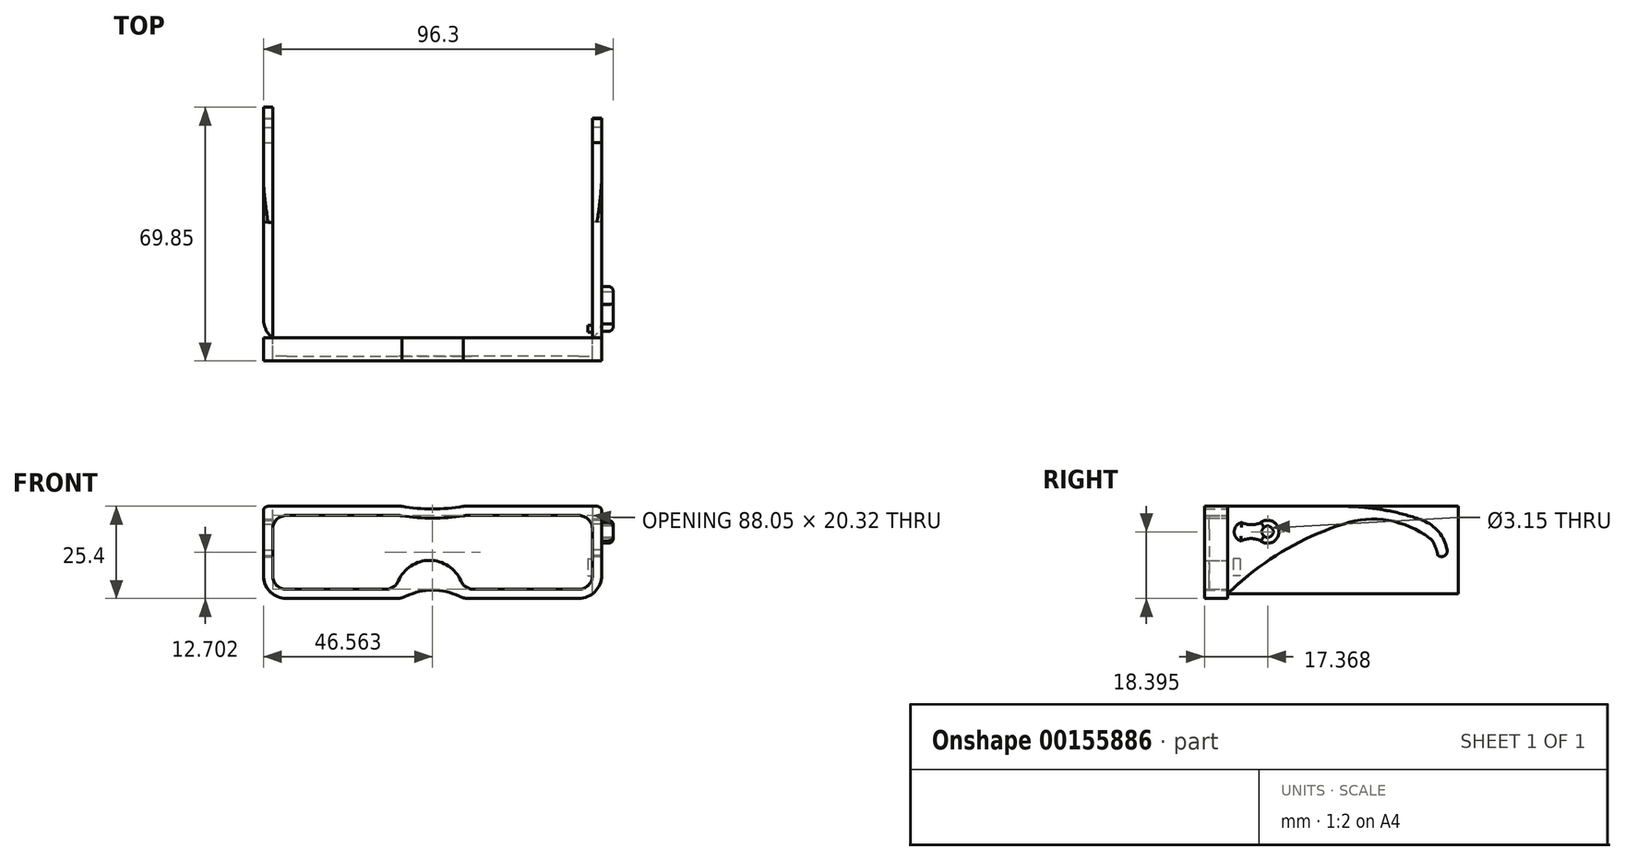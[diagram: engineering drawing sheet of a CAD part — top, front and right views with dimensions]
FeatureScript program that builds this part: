
annotation { "Feature Type Name" : "Feature", "Feature Type Description" : "" }
export const myFeature = defineFeature(function(context is Context, id is Id, definition is map)
    precondition{}
    {
        {
            var Q0;
            Q0=qCreatedBy(makeId("Front.planeOp"),FACE);
            var sketch = newSketch(context, id + "F0", { "sketchPlane" : qUnion([Q0])});
            skLineSegment(sketch, "E0.bottom", {"start": v(-73.8, 25.67) * mm, "end": v(-40.04, 25.67) * mm});
            skLineSegment(sketch, "E0.left", {"start": v(-77.61, 21.86) * mm, "end": v(-77.61, 6.62) * mm});
            skLineSegment(sketch, "E0.right", {"start": v(-39.51, 25.67) * mm, "end": v(-39.51, 0.27) * mm});
            skLineSegment(sketch, "E1", {"start": v(-31.05, 25.67) * mm, "end": v(-31.05, -0.69) * mm, "construction": true});
            skLineSegment(sketch, "E2.MirrorCS", {"start": v(11.7, 25.67) * mm, "end": v(-22.06, 25.67) * mm});
            skLineSegment(sketch, "E3.MirrorCS", {"start": v(9.17, 0.27) * mm, "end": v(-21, 0.27) * mm});
            skLineSegment(sketch, "E4.MirrorCS", {"start": v(-22.58, 25.67) * mm, "end": v(-22.58, 0.27) * mm});
            skLineSegment(sketch, "E5.MirrorCS", {"start": v(15.52, 21.86) * mm, "end": v(15.52, 6.62) * mm});
            skArc(sketch, "E6", {"start": v(-23.77, 0.9) * mm, "mid": v(-31.05, 2.58) * mm, "end": v(-38.32, 0.9) * mm});
            skLineSegment(sketch, "E7.0", {"start": v(-71.26, 23.13) * mm, "end": v(-40.37, 23.13) * mm});
            skLineSegment(sketch, "E7.2", {"start": v(9.17, 23.13) * mm, "end": v(-21.72, 23.13) * mm});
            skLineSegment(sketch, "E8.0", {"start": v(12.98, 19.32) * mm, "end": v(12.98, 6.62) * mm});
            skPoint(sketch, "E9.visualSharp", {"position": v(-22.58, 0.27) * mm});
            skArc(sketch, "E9.filletArc", {"start": v(-23.77, 0.9) * mm, "mid": v(-22.42, 0.43) * mm, "end": v(-21, 0.27) * mm});
            skPoint(sketch, "E10.visualSharp", {"position": v(-39.51, 0.27) * mm});
            skArc(sketch, "E10.filletArc", {"start": v(-41.1, 0.27) * mm, "mid": v(-39.68, 0.43) * mm, "end": v(-38.32, 0.9) * mm});
            skPoint(sketch, "E11.visualSharp", {"position": v(-77.61, 0.27) * mm});
            skArc(sketch, "E11.filletArc", {"start": v(-77.61, 6.62) * mm, "mid": v(-75.75, 2.13) * mm, "end": v(-71.26, 0.27) * mm});
            skPoint(sketch, "E12.visualSharp", {"position": v(15.52, 0.27) * mm});
            skArc(sketch, "E12.filletArc", {"start": v(9.17, 0.27) * mm, "mid": v(13.66, 2.13) * mm, "end": v(15.52, 6.62) * mm});
            skPoint(sketch, "E13.visualSharp", {"position": v(15.52, 25.67) * mm});
            skArc(sketch, "E14.filletArc", {"start": v(12.98, 19.32) * mm, "mid": v(11.86, 22.02) * mm, "end": v(9.17, 23.13) * mm});
            skPoint(sketch, "E15.visualSharp", {"position": v(-22.23, 23.13) * mm});
            skArc(sketch, "E15.filletArc", {"start": v(-21.72, 23.13) * mm, "mid": v(-22.21, 23.1) * mm, "end": v(-22.69, 23) * mm});
            skPoint(sketch, "E16.visualSharp", {"position": v(-22.58, 25.67) * mm});
            skArc(sketch, "E16.filletArc", {"start": v(-22.06, 25.67) * mm, "mid": v(-22.56, 25.64) * mm, "end": v(-23.06, 25.54) * mm});
            skPoint(sketch, "E17.visualSharp", {"position": v(-39.51, 25.67) * mm});
            skArc(sketch, "E17.filletArc", {"start": v(-39.04, 25.54) * mm, "mid": v(-39.53, 25.64) * mm, "end": v(-40.04, 25.67) * mm});
            skPoint(sketch, "E18.visualSharp", {"position": v(-39.87, 23.13) * mm});
            skArc(sketch, "E18.filletArc", {"start": v(-39.4, 23) * mm, "mid": v(-39.88, 23.1) * mm, "end": v(-40.37, 23.13) * mm});
            skArc(sketch, "E19.filletArc", {"start": v(-71.26, 23.13) * mm, "mid": v(-73.96, 22.02) * mm, "end": v(-75.07, 19.32) * mm});
            skPoint(sketch, "E20.visualSharp", {"position": v(-77.61, 25.67) * mm});
            skArc(sketch, "E21", {"start": v(-39.51, 25.67) * mm, "mid": v(-31.05, 24.94) * mm, "end": v(-22.58, 25.67) * mm});
            skArc(sketch, "E22.0", {"start": v(-39.95, 23.17) * mm, "mid": v(-31.05, 22.4) * mm, "end": v(-22.14, 23.17) * mm});
            skLineSegment(sketch, "E23.0", {"start": v(-71.26, 2.81) * mm, "end": v(-43.94, 2.81) * mm});
            skArc(sketch, "E24.0", {"start": v(-75.07, 6.62) * mm, "mid": v(-73.96, 3.93) * mm, "end": v(-71.26, 2.81) * mm});
            skLineSegment(sketch, "E25", {"start": v(-75.07, 19.32) * mm, "end": v(-75.07, 6.62) * mm});
            skLineSegment(sketch, "E26", {"start": v(-71.26, 0.27) * mm, "end": v(-41.1, 0.27) * mm});
            skLineSegment(sketch, "E27.0", {"start": v(9.17, 2.81) * mm, "end": v(-19.74, 2.81) * mm});
            skArc(sketch, "E28.filletArc", {"start": v(9.17, 2.81) * mm, "mid": v(11.86, 3.93) * mm, "end": v(12.98, 6.62) * mm});
            skArc(sketch, "E29", {"start": v(-23.24, 5.12) * mm, "mid": v(-31.84, 10.79) * mm, "end": v(-40.44, 5.12) * mm});
            skPoint(sketch, "E30.visualSharp", {"position": v(-41.1, 2.81) * mm});
            skArc(sketch, "E30.filletArc", {"start": v(-43.94, 2.81) * mm, "mid": v(-41.85, 3.44) * mm, "end": v(-40.44, 5.12) * mm});
            skPoint(sketch, "E31.visualSharp", {"position": v(-22.58, 2.81) * mm});
            skArc(sketch, "E31.filletArc", {"start": v(-23.24, 5.12) * mm, "mid": v(-21.83, 3.44) * mm, "end": v(-19.74, 2.81) * mm});
            skLineSegment(sketch, "E32", {"start": v(15.52, 21.86) * mm, "end": v(15.52, 24.4) * mm});
            skLineSegment(sketch, "E33", {"start": v(11.7, 25.67) * mm, "end": v(14.25, 25.67) * mm});
            skLineSegment(sketch, "E34", {"start": v(-73.8, 25.67) * mm, "end": v(-76.34, 25.67) * mm});
            skLineSegment(sketch, "E35", {"start": v(-77.61, 21.86) * mm, "end": v(-77.61, 24.4) * mm});
            skArc(sketch, "E36.filletArc", {"start": v(15.52, 24.4) * mm, "mid": v(15.15, 25.3) * mm, "end": v(14.25, 25.67) * mm});
            skArc(sketch, "E37.filletArc", {"start": v(-76.34, 25.67) * mm, "mid": v(-77.24, 25.3) * mm, "end": v(-77.61, 24.4) * mm});
            skSolve(sketch);
        }
        {
            var Q0;
            {var subQ1=sQuery(id+"F0.wireOp",EDGE,"E0.bottom");Q0=makeQuery(id+"F0.imprint","IMPRINT",FACE,{"disambiguationData":[TD([[makeQuery(id+"F0.imprint","IMPRINT",EDGE,{"derivedFrom":subQ1}),-1.0]])]});}
            var Q1;
            {var subQ7=sQuery(id+"F0.wireOp",EDGE,"E21");Q1=makeQuery(id+"F0.imprint","IMPRINT",FACE,{"disambiguationData":[TD([[makeQuery(id+"F0.imprint","IMPRINT",EDGE,{"derivedFrom":subQ7}),-1.0]])]});}
            var Q2;
            {var subQ12=sQuery(id+"F0.wireOp",EDGE,"E2.MirrorCS");Q2=makeQuery(id+"F0.imprint","IMPRINT",FACE,{"disambiguationData":[TD([[makeQuery(id+"F0.imprint","IMPRINT",EDGE,{"derivedFrom":subQ12}),1.0]])]});}
            var Q3;
            {var subQ0=sQuery(id+"F0.wireOp",EDGE,"E6");Q3=makeQuery(id+"F0.imprint","IMPRINT",FACE,{"disambiguationData":[TD([[makeQuery(id+"F0.imprint","IMPRINT",EDGE,{"derivedFrom":subQ0}),-1.0]])]});}
            extrude(context, id + "F1", {"entities" : qUnion([Q0, Q1, Q2, Q3]), "depth" : 6.35 * mm});
        }
        {
            var Q0;
            Q0=makeQuery(id+"F1.opExtrude","CAP_FACE",FACE,{"disambiguationData":[OSD([sQuery(id+"F0.wireOp",EDGE,"E0.bottom"),sQuery(id+"F0.wireOp",EDGE,"E0.left"),sQuery(id+"F0.wireOp",EDGE,"E0.right"),sQuery(id+"F0.wireOp",EDGE,"E2.MirrorCS"),sQuery(id+"F0.wireOp",EDGE,"E3.MirrorCS"),sQuery(id+"F0.wireOp",EDGE,"E4.MirrorCS"),sQuery(id+"F0.wireOp",EDGE,"E5.MirrorCS"),sQuery(id+"F0.wireOp",EDGE,"E6"),sQuery(id+"F0.wireOp",EDGE,"E7.0"),sQuery(id+"F0.wireOp",EDGE,"E7.2"),sQuery(id+"F0.wireOp",EDGE,"E8.0"),sQuery(id+"F0.wireOp",EDGE,"E9.filletArc"),sQuery(id+"F0.wireOp",EDGE,"E10.filletArc"),sQuery(id+"F0.wireOp",EDGE,"E11.filletArc"),sQuery(id+"F0.wireOp",EDGE,"E12.filletArc"),sQuery(id+"F0.wireOp",EDGE,"E14.filletArc"),sQuery(id+"F0.wireOp",EDGE,"E15.filletArc"),sQuery(id+"F0.wireOp",EDGE,"E16.filletArc"),sQuery(id+"F0.wireOp",EDGE,"E17.filletArc"),sQuery(id+"F0.wireOp",EDGE,"E18.filletArc"),sQuery(id+"F0.wireOp",EDGE,"E19.filletArc"),sQuery(id+"F0.wireOp",EDGE,"E21"),sQuery(id+"F0.wireOp",EDGE,"E22.0"),sQuery(id+"F0.wireOp",EDGE,"E23.0"),sQuery(id+"F0.wireOp",EDGE,"E24.0"),sQuery(id+"F0.wireOp",EDGE,"E25"),sQuery(id+"F0.wireOp",EDGE,"E26"),sQuery(id+"F0.wireOp",EDGE,"E27.0"),sQuery(id+"F0.wireOp",EDGE,"E28.filletArc"),sQuery(id+"F0.wireOp",EDGE,"E29"),sQuery(id+"F0.wireOp",EDGE,"E30.filletArc"),sQuery(id+"F0.wireOp",EDGE,"E31.filletArc"),sQuery(id+"F0.wireOp",EDGE,"E32"),sQuery(id+"F0.wireOp",EDGE,"E33"),sQuery(id+"F0.wireOp",EDGE,"E34"),sQuery(id+"F0.wireOp",EDGE,"E35"),sQuery(id+"F0.wireOp",EDGE,"E36.filletArc"),sQuery(id+"F0.wireOp",EDGE,"E37.filletArc")])],"isStart":true});
            var sketch = newSketch(context, id + "F2", { "sketchPlane" : qUnion([Q0])});
            skLineSegment(sketch, "E38.0", {"start": v(-15.52, 24.4) * mm, "end": v(-15.52, 6.62) * mm});
            skArc(sketch, "E39.0", {"start": v(-15.52, 24.4) * mm, "mid": v(-15.15, 25.3) * mm, "end": v(-14.25, 25.67) * mm});
            skArc(sketch, "E40.0", {"start": v(-9.17, 0.27) * mm, "mid": v(-13.66, 2.13) * mm, "end": v(-15.52, 6.62) * mm});
            skLineSegment(sketch, "E41.0", {"start": v(22.06, 25.67) * mm, "end": v(-14.25, 25.67) * mm});
            skLineSegment(sketch, "E42.0", {"start": v(-9.17, 0.27) * mm, "end": v(21, 0.27) * mm});
            skLineSegment(sketch, "E43.0", {"start": v(-12.98, 19.32) * mm, "end": v(-12.98, 6.62) * mm});
            skLineSegment(sketch, "E44", {"start": v(-12.98, 19.32) * mm, "end": v(-12.98, 25.67) * mm});
            skLineSegment(sketch, "E45", {"start": v(-12.98, 25.67) * mm, "end": v(-12.98, 1.54) * mm});
            skSolve(sketch);
        }
        {
            var Q0;
            {var subQ1=sQuery(id+"F2.wireOp",EDGE,"E38.0");Q0=makeQuery(id+"F2.imprint","IMPRINT",FACE,{"disambiguationData":[TD([[makeQuery(id+"F2.imprint","IMPRINT",EDGE,{"derivedFrom":subQ1}),1.0]])]});}
            extrude(context, id + "F3", {"entities" : qUnion([Q0]), "depth" : 63.5 * mm});
        }
        {
            var Q0;
            Q0=makeQuery(id+"F3.opExtrude","SWEPT_FACE",FACE,{"disambiguationData":[OSD([sQuery(id+"F2.wireOp",EDGE,"E45")])]});
            var sketch = newSketch(context, id + "F4", { "sketchPlane" : qUnion([Q0])});
            skLineSegment(sketch, "E46", {"start": v(0, 25.67) * mm, "end": v(-31.75, 25.67) * mm});
            skArc(sketch, "E47", {"start": v(-31.75, 25.67) * mm, "mid": v(-42.93, 24.69) * mm, "end": v(-53.77, 21.77) * mm});
            skArc(sketch, "E48", {"start": v(-53.77, 21.77) * mm, "mid": v(-58.16, 18.6) * mm, "end": v(-60.42, 13.69) * mm});
            skArc(sketch, "E49", {"start": v(-60.42, 13.69) * mm, "mid": v(-59.72, 12.01) * mm, "end": v(-57.91, 12.2) * mm});
            skArc(sketch, "E50", {"start": v(-56.84, 15.37) * mm, "mid": v(-57.45, 13.8) * mm, "end": v(-57.91, 12.2) * mm});
            skArc(sketch, "E51", {"start": v(-31.97, 20.82) * mm, "mid": v(-44.3, 21.77) * mm, "end": v(-55.67, 16.86) * mm});
            skArc(sketch, "E52", {"start": v(0, 1.54) * mm, "mid": v(-14.85, 13.05) * mm, "end": v(-31.97, 20.82) * mm});
            skPoint(sketch, "E53.visualSharp", {"position": v(-56.42, 16.27) * mm});
            skArc(sketch, "E53.filletArc", {"start": v(-55.67, 16.86) * mm, "mid": v(-56.35, 16.19) * mm, "end": v(-56.84, 15.37) * mm});
            skLineSegment(sketch, "E54.0", {"start": v(0, 25.67) * mm, "end": v(0, 1.54) * mm});
            skSolve(sketch);
        }
        {
            var Q0;
            {var subQ3=sQuery(id+"F4.wireOp",EDGE,"E47");Q0=makeQuery(id+"F4.imprint","IMPRINT",FACE,{"disambiguationData":[TD([[makeQuery(id+"F4.imprint","IMPRINT",EDGE,{"derivedFrom":subQ3}),-1.0]])]});}
            extrude(context, id + "F5", {"entities" : qUnion([Q0]), "operationType" : NewBodyOperationType.REMOVE, "oppositeDirection" : true, "depth" : 25.4 * mm});
        }
        {
            var Q0;
            Q0=makeQuery(id+"F1.opExtrude","CAP_FACE",FACE,{"disambiguationData":[OSD([sQuery(id+"F0.wireOp",EDGE,"E0.bottom"),sQuery(id+"F0.wireOp",EDGE,"E0.left"),sQuery(id+"F0.wireOp",EDGE,"E0.right"),sQuery(id+"F0.wireOp",EDGE,"E2.MirrorCS"),sQuery(id+"F0.wireOp",EDGE,"E3.MirrorCS"),sQuery(id+"F0.wireOp",EDGE,"E4.MirrorCS"),sQuery(id+"F0.wireOp",EDGE,"E5.MirrorCS"),sQuery(id+"F0.wireOp",EDGE,"E6"),sQuery(id+"F0.wireOp",EDGE,"E7.0"),sQuery(id+"F0.wireOp",EDGE,"E7.2"),sQuery(id+"F0.wireOp",EDGE,"E8.0"),sQuery(id+"F0.wireOp",EDGE,"E9.filletArc"),sQuery(id+"F0.wireOp",EDGE,"E10.filletArc"),sQuery(id+"F0.wireOp",EDGE,"E11.filletArc"),sQuery(id+"F0.wireOp",EDGE,"E12.filletArc"),sQuery(id+"F0.wireOp",EDGE,"E14.filletArc"),sQuery(id+"F0.wireOp",EDGE,"E15.filletArc"),sQuery(id+"F0.wireOp",EDGE,"E16.filletArc"),sQuery(id+"F0.wireOp",EDGE,"E17.filletArc"),sQuery(id+"F0.wireOp",EDGE,"E18.filletArc"),sQuery(id+"F0.wireOp",EDGE,"E19.filletArc"),sQuery(id+"F0.wireOp",EDGE,"E21"),sQuery(id+"F0.wireOp",EDGE,"E22.0"),sQuery(id+"F0.wireOp",EDGE,"E23.0"),sQuery(id+"F0.wireOp",EDGE,"E24.0"),sQuery(id+"F0.wireOp",EDGE,"E25"),sQuery(id+"F0.wireOp",EDGE,"E26"),sQuery(id+"F0.wireOp",EDGE,"E27.0"),sQuery(id+"F0.wireOp",EDGE,"E28.filletArc"),sQuery(id+"F0.wireOp",EDGE,"E29"),sQuery(id+"F0.wireOp",EDGE,"E30.filletArc"),sQuery(id+"F0.wireOp",EDGE,"E31.filletArc"),sQuery(id+"F0.wireOp",EDGE,"E32"),sQuery(id+"F0.wireOp",EDGE,"E33"),sQuery(id+"F0.wireOp",EDGE,"E34"),sQuery(id+"F0.wireOp",EDGE,"E35"),sQuery(id+"F0.wireOp",EDGE,"E36.filletArc"),sQuery(id+"F0.wireOp",EDGE,"E37.filletArc")])],"isStart":true});
            var sketch = newSketch(context, id + "F6", { "sketchPlane" : qUnion([Q0])});
            skLineSegment(sketch, "E55.0", {"start": v(75.07, 19.32) * mm, "end": v(75.07, 6.62) * mm});
            skLineSegment(sketch, "E56", {"start": v(75.07, 19.32) * mm, "end": v(75.07, 25.67) * mm});
            skLineSegment(sketch, "E57", {"start": v(75.07, 25.67) * mm, "end": v(75.07, 1.54) * mm});
            skSolve(sketch);
        }
        {
            var Q0;
            {var subQ8=makeQuery(id+"F1.opExtrude","CAP_EDGE",EDGE,{"disambiguationData":[OSD([sQuery(id+"F0.wireOp",EDGE,"E37.filletArc")])],"isStart":true});Q0=makeQuery(id+"F6.imprint","IMPRINT",FACE,{"disambiguationData":[TD([[makeQuery(id+"F6.imprint","IMPRINT",EDGE,{"derivedFrom":subQ8}),-1.0]])]});}
            extrude(context, id + "F7", {"entities" : qUnion([Q0]), "depth" : 63.5 * mm});
        }
        {
            var Q0;
            Q0=makeQuery(id+"F7.opExtrude","SWEPT_FACE",FACE,{"disambiguationData":[OSD([sQuery(id+"F6.wireOp",EDGE,"E57")])]});
            var sketch = newSketch(context, id + "F8", { "sketchPlane" : qUnion([Q0])});
            skLineSegment(sketch, "E58.0", {"start": v(0, 25.67) * mm, "end": v(31.75, 25.67) * mm});
            skArc(sketch, "E59.0", {"start": v(31.75, 25.67) * mm, "mid": v(42.93, 24.69) * mm, "end": v(53.77, 21.77) * mm});
            skArc(sketch, "E60.0", {"start": v(53.77, 21.77) * mm, "mid": v(58.16, 18.6) * mm, "end": v(60.42, 13.69) * mm});
            skArc(sketch, "E61.0", {"start": v(60.42, 13.69) * mm, "mid": v(59.72, 12.01) * mm, "end": v(57.91, 12.2) * mm});
            skArc(sketch, "E62.0", {"start": v(56.84, 15.37) * mm, "mid": v(57.45, 13.8) * mm, "end": v(57.91, 12.2) * mm});
            skArc(sketch, "E63.0", {"start": v(31.97, 20.82) * mm, "mid": v(44.3, 21.77) * mm, "end": v(55.67, 16.86) * mm});
            skArc(sketch, "E64.0", {"start": v(55.67, 16.86) * mm, "mid": v(56.35, 16.19) * mm, "end": v(56.84, 15.37) * mm});
            skArc(sketch, "E65.0", {"start": v(0, 1.54) * mm, "mid": v(14.85, 13.05) * mm, "end": v(31.97, 20.82) * mm});
            skLineSegment(sketch, "E66.0", {"start": v(0, 25.67) * mm, "end": v(0, 1.54) * mm});
            skSolve(sketch);
        }
        {
            var Q0;
            {var subQ0=sQuery(id+"F8.wireOp",EDGE,"E59.0");Q0=makeQuery(id+"F8.imprint","IMPRINT",FACE,{"disambiguationData":[TD([[makeQuery(id+"F8.imprint","IMPRINT",EDGE,{"derivedFrom":subQ0}),1.0]])]});}
            extrude(context, id + "F9", {"entities" : qUnion([Q0]), "operationType" : NewBodyOperationType.REMOVE, "oppositeDirection" : true, "depth" : 25.4 * mm});
        }
        {
            var Q0;
            {var subQ2=sQuery(id+"F0.wireOp",EDGE,"E7.0");Q0=makeQuery(id+"F0.imprint","IMPRINT",FACE,{"disambiguationData":[TD([[makeQuery(id+"F0.imprint","IMPRINT",EDGE,{"derivedFrom":subQ2}),-1.0]])]});}
            var Q1;
            {var subQ4=sQuery(id+"F0.wireOp",EDGE,"E0.right");var subQ8=sQuery(id+"F0.wireOp",EDGE,"E22.0");var subQ10=makeQuery(id+"F0.imprint","INTERSECT",VERTEX,{"derivedFrom":[subQ4,subQ8]});Q1=makeQuery(id+"F0.imprint","IMPRINT",FACE,{"disambiguationData":[TD([[makeQuery(id+"F0.imprint","IMPRINT",EDGE,{"disambiguationData":[TD([[subQ10,-1.0]])],"derivedFrom":subQ4}),1.0]])]});}
            var Q2;
            {var subQ0=sQuery(id+"F0.wireOp",EDGE,"E7.2");Q2=makeQuery(id+"F0.imprint","IMPRINT",FACE,{"disambiguationData":[TD([[makeQuery(id+"F0.imprint","IMPRINT",EDGE,{"derivedFrom":subQ0}),1.0]])]});}
            extrude(context, id + "F10", {"entities" : qUnion([Q0, Q1, Q2]), "depth" : 5.08 * mm});
        }
        {
            var Q0;
            Q0=makeQuery(id+"F3.opExtrude","SWEPT_FACE",FACE,{"disambiguationData":[OSD([sQuery(id+"F2.wireOp",EDGE,"E38.0")])]});
            var sketch = newSketch(context, id + "F11", { "sketchPlane" : qUnion([Q0])});
            skArc(sketch, "E67", {"start": v(3.93, 21.23) * mm, "mid": v(1.84, 18.72) * mm, "end": v(3.8, 16.1) * mm});
            skArc(sketch, "E68", {"start": v(3.93, 21.23) * mm, "mid": v(6.56, 20.58) * mm, "end": v(9.2, 21.23) * mm});
            skArc(sketch, "E69", {"start": v(9.2, 16.1) * mm, "mid": v(6.5, 16.78) * mm, "end": v(3.8, 16.1) * mm});
            skArc(sketch, "E70", {"start": v(9.2, 16.1) * mm, "mid": v(14.17, 18.66) * mm, "end": v(9.2, 21.23) * mm});
            skCircle(sketch, "E71", {"center": v(11.02, 18.66) * mm, "radius": 1.57 * mm});
            skSolve(sketch);
        }
        {
            var Q0;
            Q0=makeQuery(id+"F11.imprint","IMPRINT",FACE,{"disambiguationData":[TD([[makeQuery(id+"F11.imprint","IMPRINT",EDGE,{"derivedFrom":sQuery(id+"F11.wireOp",EDGE,"E67")}),1.0]])]});
            extrude(context, id + "F12", {"entities" : qUnion([Q0]), "depth" : 3.17 * mm});
        }
        {
            var Q0;
            Q0=makeQuery(id+"F12.opExtrude","CAP_EDGE",EDGE,{"disambiguationData":[OSD([sQuery(id+"F11.wireOp",EDGE,"E67")])],"isStart":false});
            var Q1;
            Q1=makeQuery(id+"F12.opExtrude","CAP_EDGE",EDGE,{"disambiguationData":[OSD([sQuery(id+"F11.wireOp",EDGE,"E68")])],"isStart":false});
            var Q2;
            Q2=makeQuery(id+"F12.opExtrude","CAP_EDGE",EDGE,{"disambiguationData":[OSD([sQuery(id+"F11.wireOp",EDGE,"E70")])],"isStart":false});
            var Q3;
            Q3=makeQuery(id+"F12.opExtrude","CAP_EDGE",EDGE,{"disambiguationData":[OSD([sQuery(id+"F11.wireOp",EDGE,"E69")])],"isStart":false});
            fillet(context, id + "F13", {"entities" : qUnion([Q0, Q1, Q2, Q3]), "radius" : 1.27 * mm, "tangentPropagation" : true, "allowEdgeOverflow" : false});
        }
        {
            var Q0;
            Q0=makeQuery(id+"F11.imprint","IMPRINT",FACE,{"disambiguationData":[TD([[makeQuery(id+"F11.imprint","IMPRINT",EDGE,{"derivedFrom":sQuery(id+"F11.wireOp",EDGE,"E71")}),1.0]])]});
            extrude(context, id + "F14", {"entities" : qUnion([Q0]), "depth" : 3.17 * mm});
        }
        {
            var Q0;
            Q0=makeQuery(id+"F3.opExtrude","SWEPT_FACE",FACE,{"disambiguationData":[OSD([sQuery(id+"F2.wireOp",EDGE,"E45")])]});
            var sketch = newSketch(context, id + "F15", { "sketchPlane" : qUnion([Q0])});
            skLineSegment(sketch, "E72.bottom", {"start": v(-3.47, 11.24) * mm, "end": v(-1.54, 11.24) * mm});
            skLineSegment(sketch, "E72.top", {"start": v(-3.47, 6.51) * mm, "end": v(-1.54, 6.51) * mm});
            skLineSegment(sketch, "E72.left", {"start": v(-3.47, 11.24) * mm, "end": v(-3.47, 6.51) * mm});
            skLineSegment(sketch, "E72.right", {"start": v(-1.54, 11.24) * mm, "end": v(-1.54, 6.51) * mm});
            skSolve(sketch);
        }
        {
            var Q0;
            Q0=makeQuery(id+"F15.imprint","IMPRINT",FACE,{"disambiguationData":[TD([[makeQuery(id+"F15.imprint","IMPRINT",EDGE,{"derivedFrom":sQuery(id+"F15.wireOp",EDGE,"E72.bottom")}),-1.0]])]});
            extrude(context, id + "F16", {"entities" : qUnion([Q0]), "depth" : 1.27 * mm});
        }
    });
